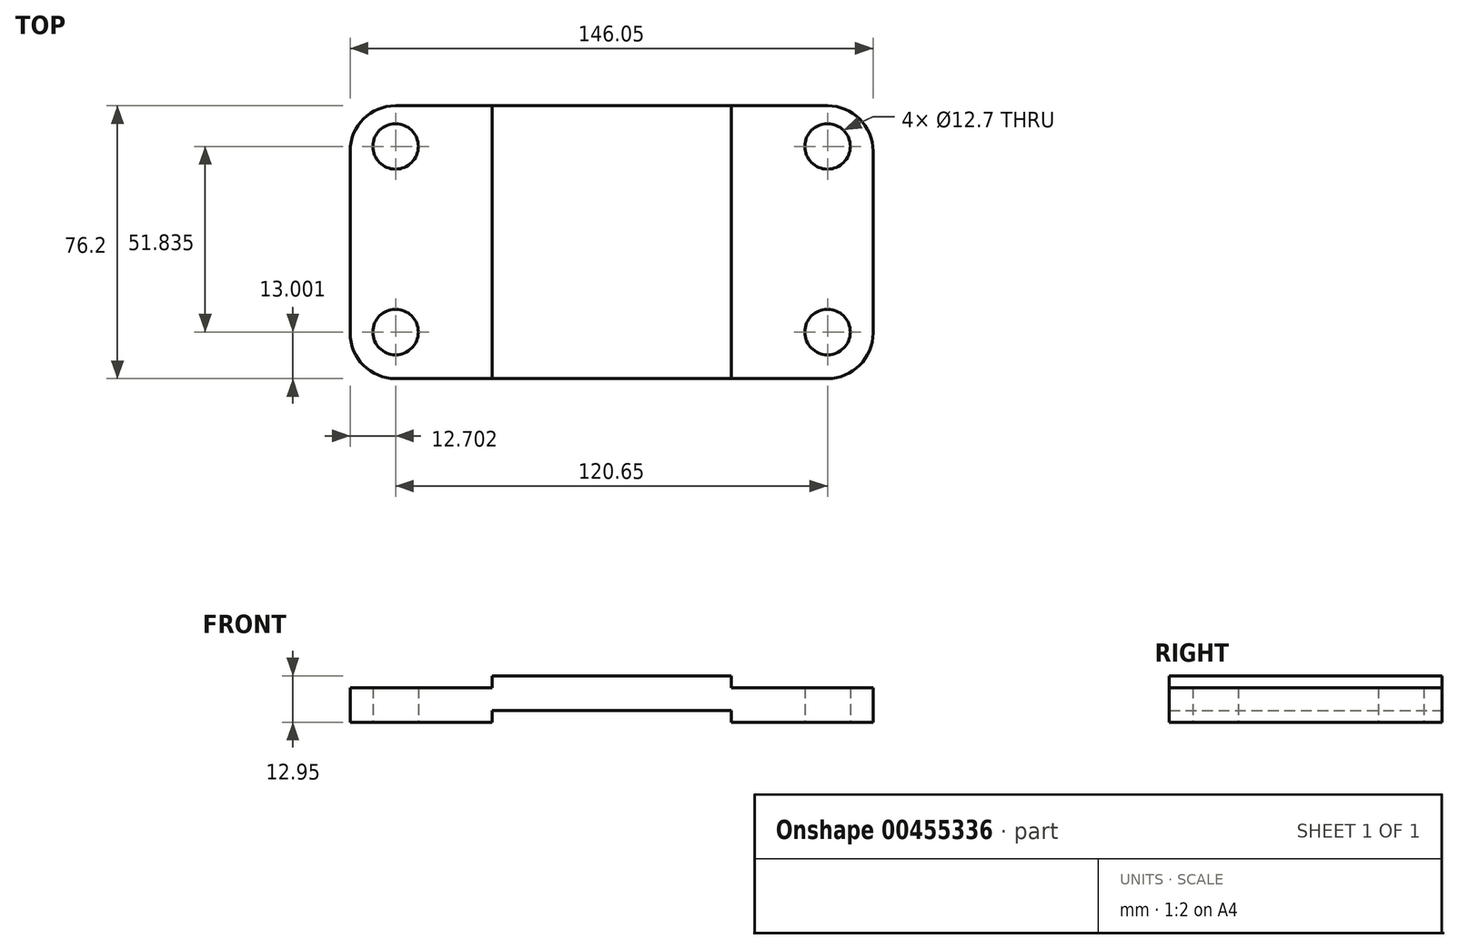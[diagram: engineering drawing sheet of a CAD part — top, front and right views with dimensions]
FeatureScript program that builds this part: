
annotation { "Feature Type Name" : "Feature", "Feature Type Description" : "" }
export const myFeature = defineFeature(function(context is Context, id is Id, definition is map)
    precondition{}
    {
        {
            var Q0;
            Q0=qCreatedBy(makeId("Front.planeOp"),FACE);
            var sketch = newSketch(context, id + "F0", { "sketchPlane" : qUnion([Q0])});
            skLineSegment(sketch, "E0", {"start": v(-76.13, 45.5) * mm, "end": v(-76.13, 35.86) * mm});
            skLineSegment(sketch, "E1", {"start": v(-76.13, 35.86) * mm, "end": v(-36.5, 35.86) * mm});
            skLineSegment(sketch, "E2", {"start": v(-76.13, 45.5) * mm, "end": v(-36.5, 45.5) * mm});
            skLineSegment(sketch, "E3", {"start": v(-36.5, 45.5) * mm, "end": v(-36.5, 48.81) * mm});
            skLineSegment(sketch, "E4", {"start": v(-36.5, 35.86) * mm, "end": v(-36.5, 39.16) * mm});
            skLineSegment(sketch, "E5", {"start": v(-36.5, 39.16) * mm, "end": v(30.3, 39.16) * mm});
            skLineSegment(sketch, "E6", {"start": v(30.3, 39.16) * mm, "end": v(30.3, 35.86) * mm});
            skLineSegment(sketch, "E7", {"start": v(-36.5, 48.81) * mm, "end": v(30.3, 48.81) * mm});
            skLineSegment(sketch, "E8", {"start": v(30.3, 48.81) * mm, "end": v(30.3, 45.5) * mm});
            skLineSegment(sketch, "E9", {"start": v(30.3, 45.5) * mm, "end": v(69.92, 45.5) * mm});
            skLineSegment(sketch, "E10", {"start": v(30.3, 35.86) * mm, "end": v(69.92, 35.86) * mm});
            skLineSegment(sketch, "E11", {"start": v(69.92, 35.86) * mm, "end": v(69.92, 45.5) * mm});
            skSolve(sketch);
        }
        {
            var Q0;
            Q0 = qSketchRegion(id + "F0", true);
            extrude(context, id + "F1", {"entities" : qUnion([Q0]), "depth" : 76.2 * mm});
        }
        {
            var Q0;
            Q0=makeQuery(id+"F1.opExtrude","CAP_EDGE",EDGE,{"disambiguationData":[OSD([sQuery(id+"F0.wireOp",EDGE,"E11")])],"isStart":true});
            var Q1;
            Q1=makeQuery(id+"F1.opExtrude","CAP_EDGE",EDGE,{"disambiguationData":[OSD([sQuery(id+"F0.wireOp",EDGE,"E11")])],"isStart":false});
            var Q2;
            Q2=makeQuery(id+"F1.opExtrude","CAP_EDGE",EDGE,{"disambiguationData":[OSD([sQuery(id+"F0.wireOp",EDGE,"E0")])],"isStart":false});
            var Q3;
            Q3=makeQuery(id+"F1.opExtrude","CAP_EDGE",EDGE,{"disambiguationData":[OSD([sQuery(id+"F0.wireOp",EDGE,"E0")])],"isStart":true});
            fillet(context, id + "F2", {"entities" : qUnion([Q0, Q1, Q2, Q3]), "radius" : 12.7 * mm, "tangentPropagation" : true, "allowEdgeOverflow" : false});
        }
        {
            var Q0;
            Q0=qCreatedBy(makeId("Top.planeOp"),FACE);
            var sketch = newSketch(context, id + "F3", { "sketchPlane" : qUnion([Q0])});
            skCircle(sketch, "E12", {"center": v(57.22, -11.36) * mm, "radius": 6.35 * mm});
            skCircle(sketch, "E13", {"center": v(57.22, -63.2) * mm, "radius": 6.35 * mm});
            skCircle(sketch, "E14", {"center": v(-63.43, -63.2) * mm, "radius": 6.35 * mm});
            skCircle(sketch, "E15", {"center": v(-63.43, -11.36) * mm, "radius": 6.35 * mm});
            skSolve(sketch);
        }
        {
            var Q0;
            Q0 = qSketchRegion(id + "F3", true);
            extrude(context, id + "F4", {"entities" : qUnion([Q0]), "operationType" : NewBodyOperationType.REMOVE, "endBound" : BoundingType.THROUGH_ALL, "depth" : 25.4 * mm});
        }
    });
